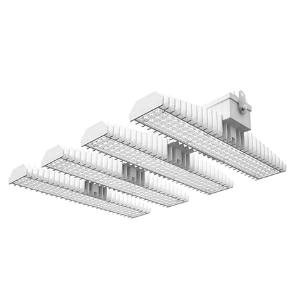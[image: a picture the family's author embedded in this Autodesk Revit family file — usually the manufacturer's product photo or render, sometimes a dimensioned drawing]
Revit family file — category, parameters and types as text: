
# Revit family: 3f_filippi_-_3f_lem_ht_concentrato_3f_filippi_-_59034_a0811_-_3f_lem_4_ht_led_120_cr_conc___vt_ed2f
name_source: partatom
category: Lighting Fixtures
units: mm (PartAtom-declared; Revit-internal decimal feet)

## family parameters
Cut with Voids When Loaded = No
Host = Face
Light Source = No
Part Type = Normal
Room Calculation Point = No
Round Connector Dimension = Use Diameter
Shared = No

## types (1)
- 3F Filippi - 3F LEM HT Concentrato (1 x LED, 19387 lm, 136 W, 4000 K)
    Apparent Load = 136 VA
    Approval mark = ENEC
    CIE Flux Codes = 83 96 99 100 100
    Color Rendering = 80
    Color Temperature = 4000 K
    Control Gear = Electronic ballast
    Default Elevation = 1800 mm
    Description = Industrial luminaire with high light output and high luminous efficiency designed with the most innovative technologies for environments with temperature up to 70°C.

ILLUMINOTECHNICAL
Luminous efficiency 100% (DLOR 99%, ULOR 1%).
Initial luminous flux of the luminaire 19387 lm.
Direct symmetric narrow distribution: the illuminated area has a elliptical shape.
Installation Interdistance Transv.D = 0.52 x hu - Long.D = 1.16 x hu.
Tabular UGR (CIE 117 - 4H-8H; S=0.25H; 70/50/20): RUG 15.6 - 19.5.
Beam angle: 31° - 73°.
Luminous efficacy 143 lm/W.
Lifetime (L93/B10): 30000 h. (tq+25°C)
Lifetime (L90/B10): 50000 h. (tq+25°C)
Lifetime (L85/B10): 80000 h. (tq+25°C)
Lifetime (L80/B10): 100000 h. (tq+25°C)
Lifetime (L85/B10): 50000 h. (tq+70°C)
Sudden decreased luminous flux after 50000 hours: 0% (C0).
Photobiological safety in compliance with IEC/TR 62778: RG0 risk exempt, (IEC 62471).
In compliance with IEC/EN 62722-2-1 - IEC/EN 62717 standards.
Luminous flux at +70°C: -13.5%.

SOURCE
4 Mid-Power linear LED modules 30W/840.
Energy efficiency class (UE 2019/2020 - UE 2019/2015): C.
CIE 13.3 Colour rendering index: CRI >80 (R9 <50%).
IES TM-30 Fidelity Index: Rf = 84 Rg = 95.
CCT nominal colour temperature 4000 K.
Colour initial tolerance (MacAdam): SDCM 3.

MECHANICAL
Passive modular heatsinks in die-casted aluminium, painted in white colour.
To optimize the thermal management of the LED module, the heatsinks are oversized and provided with self-cleaning of cooling fins.
Wiring body in aluminium and galvanised steel anchored solidly to the sinks and thermally separated.
3F Lens lenses with high luminous efficiency, transparent polycarbonate, fixed to the LED modules.
Fixing brackets in stainless steel.
Luminaire with limited surface temperature. - D - (EN 60598-2-24)
Dimensions: 757x542 mm, height 133 mm. Weight 18.188 kg.
IP65 protection degree.
Mechanical strength to impacts IK08 (5 joule).
Glow-wire test resistance 850°C.

ELECTRICAL
Halogen Free electronic wiring 230V-50/60Hz, power factor 0.97, THD <25%, constant output current, class I, 2 driver.
Power of the luminaire 136 W.
CE - IEC 60598-1 - EN 60598-1.
SAFE FLICKER: PstLM=<1 and SVM=<0.4 (IEC TR 61547-1 and IEC TR 63158), to ensure a more comfortable and safe light.
Luminaire compliant with EN 60598-2-22 for power supply from a centralised emergency system CPSS (Central Power Supply System), not incorporated in the luminaire - high risk areas excluded. The default power and flux are 100% in AC and 100% in DC.
Ambient temperature from -30°C to +70°C.
Temperature class T6 max 85°C.
Quick connection via M20 3P connector with 9-13 mm tightening range.
Power unit positioned on a separate compartment by the LED module to ensure optimum temperatures of cabling components, to be inspectable and maintainable.
Relative humidity UR: <85%.

INSTALLATION
Ceiling / Suspended / Wall.
All accessories dedicated to this product are available on the Catalog and on our website www.3F-Filippi.com.

ACCESSORIES
A0811 - VT transparent glass, tempered, not flammable, with sealing gasket.
One required for each light module. The pack contains 10 pieces.

APPLICATIONS
In commercial environments, exhibition and industrial areas, stores, open areas.
Applications with high ambient temperature up to 70°C.

WARNING
Fixture not suitable for cold stores with an ambient temperature <0°C and/or relative humidity >85%.
Luminaire designed for disposal/recycling at end-of-life.
Replaceable (LED only) light source by a professional. Replaceable control gear by a professional.
    Height = 133 mm  [stored 0.436352 ft]
    Lamp = 1 x LED
    Lamp Light Flux = 19387 lm
    Lamp Power = 136 W
    Lamp count = 1
    Length = 757 mm
    Lifetime = 50000 h
    Luminous efficacy = 143 lm/W
    Manufacturer = 3F Filippi
    ModVariant = No
    Model = 3F Filippi - 59034+A0811 - 3F LEM 4 HT LED 120 CR CONC + VT
    Mounting Place = Ceiling
    Mounting Type = Pendant
    Number of Poles = 1
    OnlyDefault = Yes
    Power Factor = 1
    Product Name = 3F Filippi - 3F LEM HT Concentrato
    Product group = pendant luminaire
    ProductGroupID = 9
    Protection Class = Protection class I
    Protection Degree = IP 65
    RLX_Detail_Level = 1
    RLX_Emergency_Light_Flux = 0 lm
    RLX_Emergency_Type = 0
    RLX_Emergency_Type_DB = No
    RlxData = <blob elided: 117905 chars, md5=67631ac2>
    Socket = socket
    Standby Power = 0 W
    System Light Flux = 19387 lm
    System Power = 136 W
    Type Comments = Product without accessories
    Type Image = 3f_filippi_-_lem_4__a0811.jpg
    URL = http://relux.com
    VarID = ---
    Voltage = 0 V
    Weight = 0.00 kg
    Width = 542 mm

note: [stored X ft] marks values corroborated as IEEE doubles in the binary element streams (Revit-internal decimal feet)

## geometry (parser evidence)
native form markers: Blend x4, Sweep x14
no freeform markers — native parametric forms only
